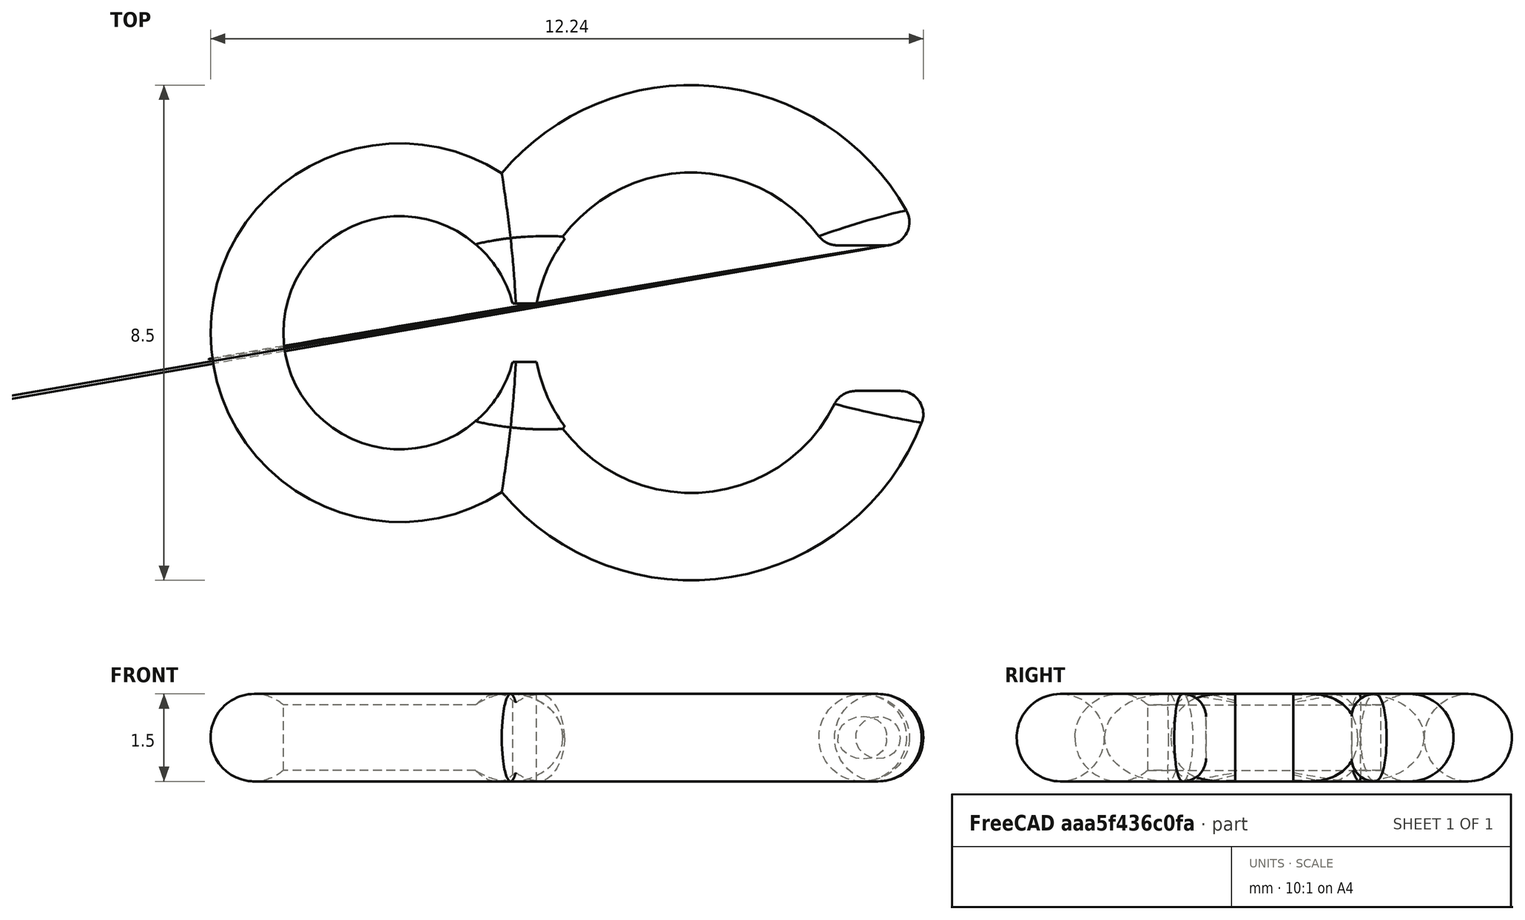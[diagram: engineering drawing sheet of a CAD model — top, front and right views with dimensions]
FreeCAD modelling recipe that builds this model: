
FCSTD DOCUMENT  (FreeCAD 0.16R)
Label: Auriculares Edu V4
License: All rights reserved
LicenseURL: http://en.wikipedia.org/wiki/All_rights_reserved
objects: Part::Cut×4, Part::Torus×2, Part::Cylinder×2, Part::Box×2, PartDesign::Fillet×2, Part::MultiFuse×1
note: 13 computed .brp shape members not serialized (recipe doc carries the construction recipe); baked Part::Feature solids carry a one-line shape summary decoded from their .brp

FEATURE [Part::Torus] Torus  label="Toro"
  Angle1 = -180
  Angle2 = 180
  Angle3 = 360
  Radius1 = 3.5
  Radius2 = 0.75
FEATURE [Part::Torus] Torus001  label="Toro001"
  Angle1 = -180
  Angle2 = 180
  Angle3 = 360
  Placement = pos=(-5,0,0) rot=(0,0,1;0rad)
  Radius1 = 2.5
  Radius2 = 0.75
FEATURE [Part::MultiFuse] Fusion
  Shapes = -> [Torus001,Torus]
FEATURE [Part::Cylinder] Cylinder  label="Cilindro"
  Angle = 360
  Height = 10
  Placement = pos=(-5,0,-4) rot=(0,0,1;0rad)
  Radius = 2
FEATURE [Part::Cut] Cut
  Base = -> Fusion
  Tool = -> Cylinder
FEATURE [Part::Cylinder] Cylinder001  label="Cilindro001"
  Angle = 360
  Height = 10
  Placement = pos=(0,0,-9) rot=(0,0,1;0rad)
  Radius = 2.7
FEATURE [Part::Cut] Cut001
  Base = -> Cut
  Tool = -> Cylinder001
FEATURE [Part::Box] Box  label="Cubo"
  Height = 5
  Length = 3
  Placement = pos=(-4,-0.5,-3) rot=(0,0,1;0rad)
  Width = 1
FEATURE [Part::Cut] Cut002
  Base = -> Cut001
  Tool = -> Box
FEATURE [Part::Box] Box001  label="Cubo001"
  Height = 10
  Length = 4
  Placement = pos=(1,-1,-6) rot=(0,0,1;0rad)
  Width = 2.5
FEATURE [Part::Cut] Cut003
  Base = -> Cut002
  Tool = -> Box001
FEATURE [PartDesign::Fillet] Fillet
  Base = -> Cut003 [Edge12]
  Radius = 0.4
FEATURE [PartDesign::Fillet] Fillet001
  Base = -> Fillet [Edge25]
  Radius = 0.4
